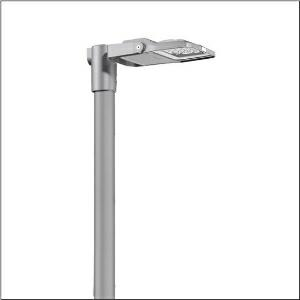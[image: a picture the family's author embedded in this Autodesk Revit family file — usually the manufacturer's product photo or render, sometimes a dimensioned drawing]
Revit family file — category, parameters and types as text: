
# Revit family: floodlight_fl_21_iq_micro___pl43_5xa7762a4a3a_9a39
name_source: partatom
category: Lighting Fixtures
units: mm (PartAtom-declared; Revit-internal decimal feet)

## family parameters
Cut with Voids When Loaded = No
Host = Face
Light Source = No
Part Type = Normal
Room Calculation Point = No
Round Connector Dimension = Use Diameter
Shared = No

## types (1)
- --- (1 x LED, 3170 lm, 23.1 W, 4000K)
    Apparent Load = 23 VA
    CIE Flux Codes = 29 80 99 100 100
    Color Rendering = 70
    Color Temperature = 4000K
    Default Elevation = 1800 mm
    Description = Floodlight FL 21 iQ micro, floodlight, primary light control with lens, of PMMA, primary optical cover: protective disc, of toughened safety glass, transparent, light distribution: PL43, light emission: direct distribution, installation type: surface-mounted, LED, High Power LED, rated luminous flux: 3.170lm, luminous efficacy: 137lm/W, light colour: 740, colour temperature: 4000K, control gear: iQ Street-Remote/DALI, control: Auto-Match, Temp-Guard, Night-Set, Smart-Wire, Desk-Remote (wireless, voltage-free reading and setting of iQ features in the workshop via application-optimized NFC function/RFID function), optimised constant luminous flux control (CLO 2.0), Street-Remote, with terminal, 6-pole, mains connection: 220..240V, AC, 50/60Hz, start of lifetime: 23W, end of service life: 24W, reduction: 11W, luminaire housing, of diecast aluminium, powder-coated, Siteco® metallic grey (DB 702S), corrosivity category C5 mid according to DIN EN ISO 12944, suitable for swimming pools, chlorine-resistant, sealing non-destructively replaceable, please order mast flange separately, mast bracket, of steel, galvanised, powder-coated, Siteco® metallic grey (DB 702S), protection rating (complete): IP66, insulation class (complete): insulation class II (safety insulation), certification: CE, ENEC, VDE, protection symbol: D, impact resistance: IK07, permissible operating ambient temperature: -40..+40°C, permissible operating ambient temperature for outdoor applications: -40..+50°C, standard: DIN EN 12944, LABS conformity tested according to VDMA 24364:2018-05, packaging unit: 1 piece

Light Distribution: PL43
    Height = 65 mm
    Lamp = 1 x LED
    Lamp Light Flux = 3170 lm
    Lamp Power = 23.1 W
    Lamp count = 1
    Length = 312 mm
    Luminous efficacy = 137 lm/W
    Manufacturer = Siteco
    ModVariant = No
    Model = 5XA7762A4A3A
    Number of Poles = 1
    OnlyDefault = Yes
    Power Factor = 1
    Product Name = Floodlight FL 21 iQ micro | PL43
    Product group = floodlight | pylon annexe
    ProductGroupID = 6200
    Protection Class = Protection class II
    Protection Degree = IP 66
    RLX_Detail_Level = 1
    RLX_Emergency_Light_Flux = 0 lm
    RLX_Emergency_Type = 0
    RLX_Emergency_Type_DB = No
    RlxData = <blob elided: 101857 chars, md5=94e24376>
    Socket = socket
    Standby Power = 0 W
    System Light Flux = 3170 lm
    System Power = 23 W
    Type Comments = factory setting: luminous flux: 100 % | dim-lin: 254 | 455 mA
    Type Image = l_1007121.jpg
    URL = http://relux.com
    VarID = @adj_176468
    Voltage = 0 V
    Weight = 0.00 kg
    Width = 230 mm

## geometry (parser evidence)
native form markers: Blend x4, Sweep x13
no freeform markers — native parametric forms only
